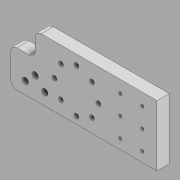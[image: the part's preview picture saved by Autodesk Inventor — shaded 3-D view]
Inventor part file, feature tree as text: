
AUTODESK INVENTOR PART (.ipt)
format: ipt  version: 2020 (Build 240168000, 168)  size: 157,184 bytes
history: native  units: in
note: dims shown in document units (in); Inventor stores cm internally (conversion verified against a paired STEP export)
features: sketch x4, hole x3, extrude x1, other x1, pattern_circular x1, pattern_linear x1, fillet x1
ambient origin geometry x8: Origin, YZ Plane, XZ Plane, XY Plane, X Axis, Y Axis, Z Axis, Center Point
bodies: Solid1 (feature_tree)
feature tree (12):
  extrude  "Extrusion1"  Depth=2.5in
  hole  "Hole1"  [1 undecoded]
  hole  "Hole2"  [1 undecoded]
  other  "Work Axis1"
  pattern_circular  "Circular Pattern1"  [2 undecoded]
  hole  "Hole3"  [1 undecoded]
  pattern_linear  "Rectangular Pattern1"  Spacing1=0.4in  [1 undecoded]
  fillet  "Fillet1"  Radius=1.8in
  sketch  "Sketch1"  dims[d0=6.0in d1=2.5in]
  sketch  "Sketch2"  dims[d2=5.0in d3=1.5in]
  sketch  "Sketch3"  dims[d4=0.5in d5=0.0in d6=5.0in]
  sketch  "Sketch4"  dims[d7=0.4in d8=0.5in d9=0.4in d10=0.4in d11=0.25in d12=0.75in d13=0.375in d14=0.25in d15=0.5635in d16=1.0in d17=0.8108in d18=1.8in d19=3.3in d20=1.2in d25=0.188in d26=0.75in d27=0.375in d28=0.25in d29=0.5635in d30=1.0in d31=0.8108in d32=1.5in d34=3.1496in d35=360.0deg d37=2.0in d38=0.125in d39=0.75in d40=0.375in d41=0.25in d42=0.5635in d43=1.0in d44=0.8108in d45=0.7874in d47=0.9in d48=1.1811in d50=0.8in d51=0.25in]
note: 6 required parameter values undecoded (feature->parameter linkage not recoverable at this tier; creation-order binding heuristic only, values carry confidence <= 0.55)
